# Revit family: Sink-Vessel-Lavatory-KOHLER-Antilia-K-2369
name_source: partatom
category: Plumbing Fixtures
revit_build: Autodesk Revit 2017 (Build: 20160225_1515(x64)
units: mm (PartAtom-declared; Revit-internal decimal feet)

## family parameters
Cut with Voids When Loaded = No
Host = Face
OmniClass Number = 23.45.05.14.14
Part Type = Normal
Room Calculation Point = No
Round Connector Dimension = Use Diameter
Shared = No

## types (1)
- B11-Ice
    ADA Compliant = Yes
    Assembly Code = D2010400
    CW Connection = No
    Cold Water Inlet = Cold Water Inlet
    Date Modified = 08/26/2021
    Default Elevation = 36"
    Description = Wading Pool glass bathroom sink
    Drain Included = No
    Finish = Kohler-Glass-B11-Ice
    HW Connection = No
    Height = 2 3/4"
    Hot Water Inlet = Hot Water Inlet
    Length = 28 1/16"
    Manufacturer = KOHLER Co.
    MasterFormat 1995 = 15410
    MasterFormat 2004 = 22.41.16
    Material = Glass
    Model = K-2369-CG-B11
    Product Documentation Link = https://www.us.kohler.com
    Product Name = Antilia
    Product Page URL = http://www.us.kohler.com
    URL = https://www.us.kohler.com
    Vent Connection = No
    Waste Connection = Yes
    Waste Water Outlet = Waste Water Outlet
    WaterSense Certified = No
    Width = 17 1/16"

## geometry (parser evidence)
native form markers: Sweep x4
no freeform markers — native parametric forms only
